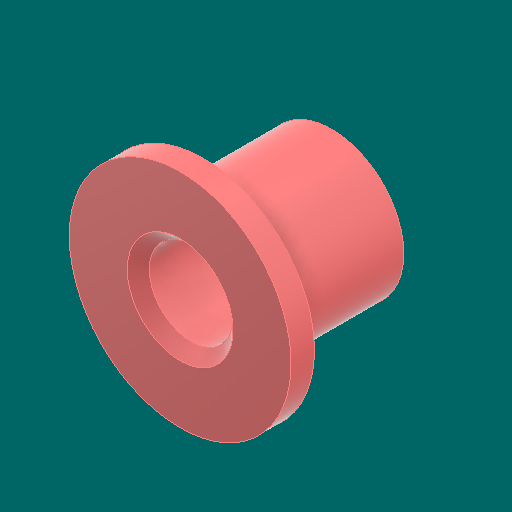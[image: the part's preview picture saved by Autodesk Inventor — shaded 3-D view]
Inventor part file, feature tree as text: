
AUTODESK INVENTOR PART (.ipt)
format: ipt  version: 2023.1 (Build 271208000, 208)  size: 121,344 bytes
history: native  units: in
note: dims shown in document units (in); Inventor stores cm internally (conversion verified against a paired STEP export)
features: other x3, sketch x2
ambient origin geometry x8: Origin, YZ Plane, XZ Plane, XY Plane, X Axis, Y Axis, Z Axis, Center Point
bodies: Solid1 (feature_tree)
feature tree (5):
  other  "bearingsleeve.ipt"
  other  "Solid1::bearingsleeve.ipt"
  other  "TaggingFeature1"
  sketch  "Sketch1"  dims[d0=0.3937in]
  sketch  "Sketch2"
